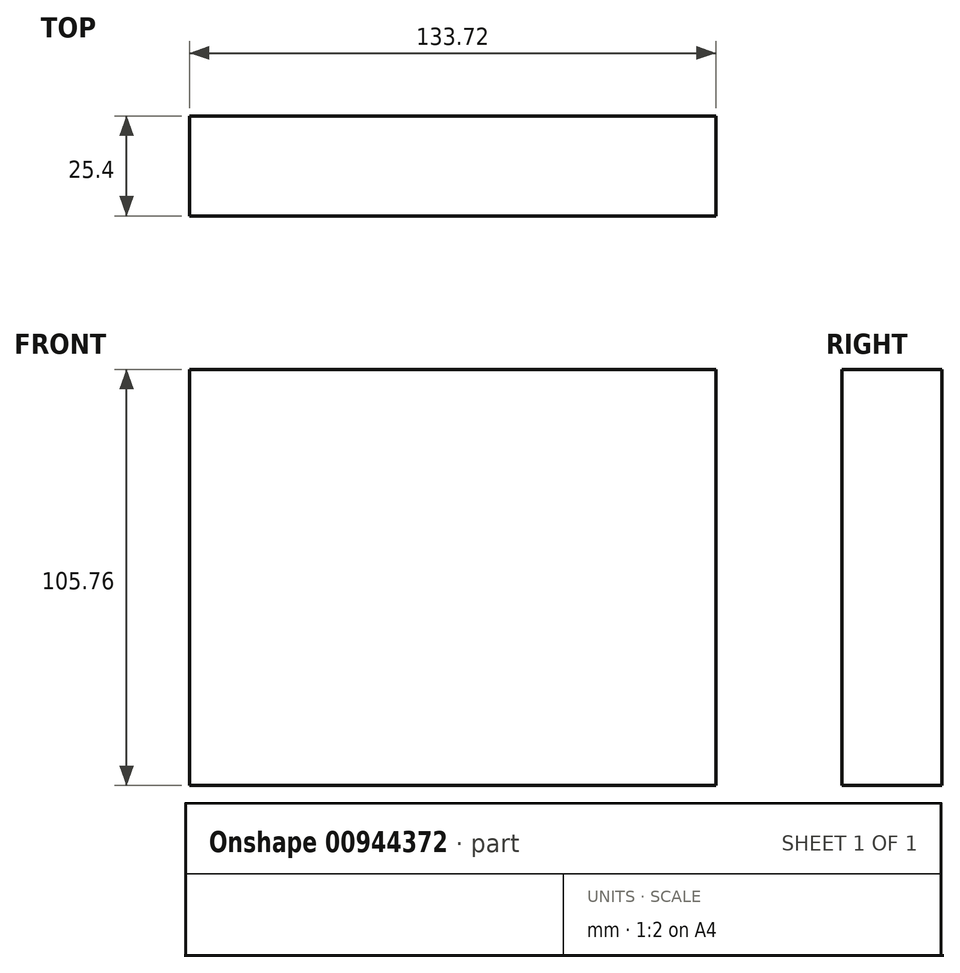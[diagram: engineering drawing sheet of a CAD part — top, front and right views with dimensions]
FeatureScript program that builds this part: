
annotation { "Feature Type Name" : "Feature", "Feature Type Description" : "" }
export const myFeature = defineFeature(function(context is Context, id is Id, definition is map)
    precondition{}
    {
        {
            var Q0;
            Q0=qCreatedBy(makeId("Front.planeOp"),FACE);
            var sketch = newSketch(context, id + "F0", { "sketchPlane" : qUnion([Q0])});
            skLineSegment(sketch, "E0.bottom", {"start": v(-65.46, 51.48) * mm, "end": v(68.26, 51.48) * mm});
            skLineSegment(sketch, "E0.top", {"start": v(-65.46, -54.28) * mm, "end": v(68.26, -54.28) * mm});
            skLineSegment(sketch, "E0.left", {"start": v(-65.46, 51.48) * mm, "end": v(-65.46, -54.28) * mm});
            skLineSegment(sketch, "E0.right", {"start": v(68.26, 51.48) * mm, "end": v(68.26, -54.28) * mm});
            skSolve(sketch);
        }
        {
            var Q0;
            Q0=makeQuery(id+"F0.imprint","IMPRINT",FACE,{"disambiguationData":[TD([[makeQuery(id+"F0.imprint","IMPRINT",EDGE,{"derivedFrom":sQuery(id+"F0.wireOp",EDGE,"E0.bottom")}),-1.0]])]});
            extrude(context, id + "F1", {"entities" : qUnion([Q0]), "depth" : 25.4 * mm, "offsetDistance" : 25.4 * mm});
        }
    });
